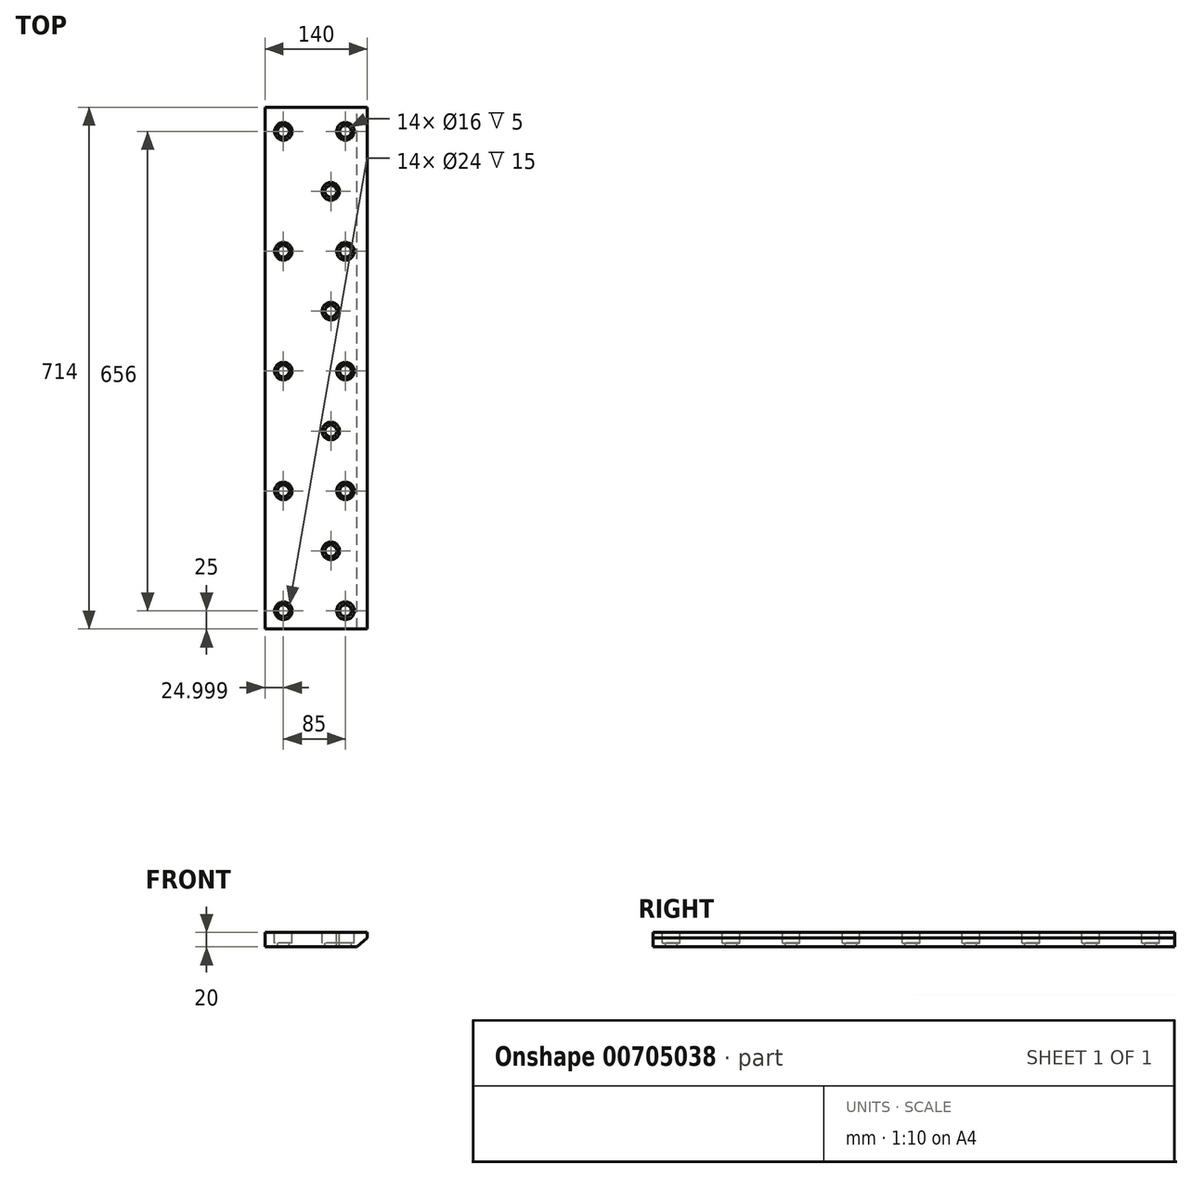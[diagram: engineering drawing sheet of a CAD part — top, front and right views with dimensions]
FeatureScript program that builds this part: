
annotation { "Feature Type Name" : "Feature", "Feature Type Description" : "" }
export const myFeature = defineFeature(function(context is Context, id is Id, definition is map)
    precondition{}
    {
        {
            var Q0;
            Q0=qCreatedBy(makeId("Front.planeOp"),FACE);
            var sketch = newSketch(context, id + "F0", { "sketchPlane" : qUnion([Q0])});
            skLineSegment(sketch, "E0", {"start": v(-96.72, 31.12) * mm, "end": v(43.28, 31.12) * mm});
            skLineSegment(sketch, "E1", {"start": v(43.28, 31.12) * mm, "end": v(43.28, 23.12) * mm});
            skLineSegment(sketch, "E2", {"start": v(43.28, 23.12) * mm, "end": v(28.98, 11.12) * mm});
            skLineSegment(sketch, "E3", {"start": v(28.98, 11.12) * mm, "end": v(-96.72, 11.12) * mm});
            skLineSegment(sketch, "E4", {"start": v(-96.72, 11.12) * mm, "end": v(-96.72, 31.12) * mm});
            skSolve(sketch);
        }
        {
            var Q0;
            Q0=makeQuery(id+"F0.imprint","IMPRINT",FACE,{"disambiguationData":[TD([[makeQuery(id+"F0.imprint","IMPRINT",EDGE,{"derivedFrom":sQuery(id+"F0.wireOp",EDGE,"E0")}),-1.0]])]});
            extrude(context, id + "F1", {"entities" : qUnion([Q0]), "depth" : 714 * mm, "offsetDistance" : 25 * mm});
        }
        {
            var Q0;
            Q0=makeQuery(id+"F1.opExtrude","SWEPT_FACE",FACE,{"disambiguationData":[OSD([sQuery(id+"F0.wireOp",EDGE,"E0")])]});
            var sketch = newSketch(context, id + "F2", { "sketchPlane" : qUnion([Q0])});
            skCircle(sketch, "E5", {"center": v(13.28, -689) * mm, "radius": 8 * mm});
            skCircle(sketch, "E6", {"center": v(-71.72, -689) * mm, "radius": 8 * mm});
            skCircle(sketch, "E7", {"center": v(-6.72, -607) * mm, "radius": 8 * mm});
            skCircle(sketch, "E8", {"center": v(13.28, -525) * mm, "radius": 8 * mm});
            skCircle(sketch, "E9", {"center": v(13.28, -361) * mm, "radius": 8 * mm});
            skCircle(sketch, "E10", {"center": v(13.28, -197) * mm, "radius": 8 * mm});
            skCircle(sketch, "E11", {"center": v(13.28, -33) * mm, "radius": 8 * mm});
            skCircle(sketch, "E12", {"center": v(-6.72, -443) * mm, "radius": 8 * mm});
            skCircle(sketch, "E13", {"center": v(-6.72, -279) * mm, "radius": 8 * mm});
            skCircle(sketch, "E14", {"center": v(-6.72, -115) * mm, "radius": 8 * mm});
            skCircle(sketch, "E15", {"center": v(-71.72, -525) * mm, "radius": 8 * mm});
            skCircle(sketch, "E16", {"center": v(-71.72, -361) * mm, "radius": 8 * mm});
            skCircle(sketch, "E17", {"center": v(-71.72, -197) * mm, "radius": 8 * mm});
            skCircle(sketch, "E18", {"center": v(-71.72, -33) * mm, "radius": 8 * mm});
            skCircle(sketch, "E19", {"center": v(13.28, -689) * mm, "radius": 12 * mm});
            skCircle(sketch, "E20", {"center": v(-71.72, -689) * mm, "radius": 12 * mm});
            skCircle(sketch, "E21", {"center": v(-6.72, -607) * mm, "radius": 12 * mm});
            skCircle(sketch, "E22", {"center": v(13.28, -525) * mm, "radius": 12 * mm});
            skCircle(sketch, "E23", {"center": v(-71.72, -525) * mm, "radius": 12 * mm});
            skCircle(sketch, "E24", {"center": v(-6.72, -443) * mm, "radius": 12 * mm});
            skCircle(sketch, "E25", {"center": v(13.28, -361) * mm, "radius": 12 * mm});
            skCircle(sketch, "E26", {"center": v(-71.72, -361) * mm, "radius": 12 * mm});
            skCircle(sketch, "E27", {"center": v(-6.72, -279) * mm, "radius": 12 * mm});
            skCircle(sketch, "E28", {"center": v(-71.72, -197) * mm, "radius": 12 * mm});
            skCircle(sketch, "E29", {"center": v(13.28, -197) * mm, "radius": 12 * mm});
            skCircle(sketch, "E30", {"center": v(-6.72, -115) * mm, "radius": 12 * mm});
            skCircle(sketch, "E31", {"center": v(13.28, -33) * mm, "radius": 12 * mm});
            skCircle(sketch, "E32", {"center": v(-71.72, -33) * mm, "radius": 12 * mm});
            skSolve(sketch);
        }
        {
            var Q0;
            Q0=makeQuery(id+"F2.imprint","IMPRINT",FACE,{"disambiguationData":[TD([[makeQuery(id+"F2.imprint","IMPRINT",EDGE,{"derivedFrom":sQuery(id+"F2.wireOp",EDGE,"E5")}),1.0]])]});
            var Q1;
            Q1=makeQuery(id+"F2.imprint","IMPRINT",FACE,{"disambiguationData":[TD([[makeQuery(id+"F2.imprint","IMPRINT",EDGE,{"derivedFrom":sQuery(id+"F2.wireOp",EDGE,"E6")}),1.0]])]});
            var Q2;
            Q2=makeQuery(id+"F2.imprint","IMPRINT",FACE,{"disambiguationData":[TD([[makeQuery(id+"F2.imprint","IMPRINT",EDGE,{"derivedFrom":sQuery(id+"F2.wireOp",EDGE,"E7")}),1.0]])]});
            var Q3;
            Q3=makeQuery(id+"F2.imprint","IMPRINT",FACE,{"disambiguationData":[TD([[makeQuery(id+"F2.imprint","IMPRINT",EDGE,{"derivedFrom":sQuery(id+"F2.wireOp",EDGE,"E8")}),1.0]])]});
            var Q4;
            Q4=makeQuery(id+"F2.imprint","IMPRINT",FACE,{"disambiguationData":[TD([[makeQuery(id+"F2.imprint","IMPRINT",EDGE,{"derivedFrom":sQuery(id+"F2.wireOp",EDGE,"E15")}),1.0]])]});
            var Q5;
            Q5=makeQuery(id+"F2.imprint","IMPRINT",FACE,{"disambiguationData":[TD([[makeQuery(id+"F2.imprint","IMPRINT",EDGE,{"derivedFrom":sQuery(id+"F2.wireOp",EDGE,"E12")}),1.0]])]});
            var Q6;
            Q6=makeQuery(id+"F2.imprint","IMPRINT",FACE,{"disambiguationData":[TD([[makeQuery(id+"F2.imprint","IMPRINT",EDGE,{"derivedFrom":sQuery(id+"F2.wireOp",EDGE,"E9")}),1.0]])]});
            var Q7;
            Q7=makeQuery(id+"F2.imprint","IMPRINT",FACE,{"disambiguationData":[TD([[makeQuery(id+"F2.imprint","IMPRINT",EDGE,{"derivedFrom":sQuery(id+"F2.wireOp",EDGE,"E16")}),1.0]])]});
            var Q8;
            Q8=makeQuery(id+"F2.imprint","IMPRINT",FACE,{"disambiguationData":[TD([[makeQuery(id+"F2.imprint","IMPRINT",EDGE,{"derivedFrom":sQuery(id+"F2.wireOp",EDGE,"E13")}),1.0]])]});
            var Q9;
            Q9=makeQuery(id+"F2.imprint","IMPRINT",FACE,{"disambiguationData":[TD([[makeQuery(id+"F2.imprint","IMPRINT",EDGE,{"derivedFrom":sQuery(id+"F2.wireOp",EDGE,"E10")}),1.0]])]});
            var Q10;
            Q10=makeQuery(id+"F2.imprint","IMPRINT",FACE,{"disambiguationData":[TD([[makeQuery(id+"F2.imprint","IMPRINT",EDGE,{"derivedFrom":sQuery(id+"F2.wireOp",EDGE,"E17")}),1.0]])]});
            var Q11;
            Q11=makeQuery(id+"F2.imprint","IMPRINT",FACE,{"disambiguationData":[TD([[makeQuery(id+"F2.imprint","IMPRINT",EDGE,{"derivedFrom":sQuery(id+"F2.wireOp",EDGE,"E14")}),1.0]])]});
            var Q12;
            Q12=makeQuery(id+"F2.imprint","IMPRINT",FACE,{"disambiguationData":[TD([[makeQuery(id+"F2.imprint","IMPRINT",EDGE,{"derivedFrom":sQuery(id+"F2.wireOp",EDGE,"E11")}),1.0]])]});
            var Q13;
            Q13=makeQuery(id+"F2.imprint","IMPRINT",FACE,{"disambiguationData":[TD([[makeQuery(id+"F2.imprint","IMPRINT",EDGE,{"derivedFrom":sQuery(id+"F2.wireOp",EDGE,"E18")}),1.0]])]});
            extrude(context, id + "F3", {"entities" : qUnion([Q0, Q1, Q2, Q3, Q4, Q5, Q6, Q7, Q8, Q9, Q10, Q11, Q12, Q13]), "operationType" : NewBodyOperationType.REMOVE, "oppositeDirection" : true, "depth" : 20 * mm, "offsetDistance" : 25 * mm});
        }
        {
            var Q0;
            Q0=makeQuery(id+"F2.imprint","IMPRINT",FACE,{"disambiguationData":[TD([[makeQuery(id+"F2.imprint","IMPRINT",EDGE,{"derivedFrom":sQuery(id+"F2.wireOp",EDGE,"E6")}),-1.0]])]});
            var Q1;
            Q1=makeQuery(id+"F2.imprint","IMPRINT",FACE,{"disambiguationData":[TD([[makeQuery(id+"F2.imprint","IMPRINT",EDGE,{"derivedFrom":sQuery(id+"F2.wireOp",EDGE,"E5")}),-1.0]])]});
            var Q2;
            Q2=makeQuery(id+"F2.imprint","IMPRINT",FACE,{"disambiguationData":[TD([[makeQuery(id+"F2.imprint","IMPRINT",EDGE,{"derivedFrom":sQuery(id+"F2.wireOp",EDGE,"E7")}),-1.0]])]});
            var Q3;
            Q3=makeQuery(id+"F2.imprint","IMPRINT",FACE,{"disambiguationData":[TD([[makeQuery(id+"F2.imprint","IMPRINT",EDGE,{"derivedFrom":sQuery(id+"F2.wireOp",EDGE,"E8")}),-1.0]])]});
            var Q4;
            Q4=makeQuery(id+"F2.imprint","IMPRINT",FACE,{"disambiguationData":[TD([[makeQuery(id+"F2.imprint","IMPRINT",EDGE,{"derivedFrom":sQuery(id+"F2.wireOp",EDGE,"E15")}),-1.0]])]});
            var Q5;
            Q5=makeQuery(id+"F2.imprint","IMPRINT",FACE,{"disambiguationData":[TD([[makeQuery(id+"F2.imprint","IMPRINT",EDGE,{"derivedFrom":sQuery(id+"F2.wireOp",EDGE,"E12")}),-1.0]])]});
            var Q6;
            Q6=makeQuery(id+"F2.imprint","IMPRINT",FACE,{"disambiguationData":[TD([[makeQuery(id+"F2.imprint","IMPRINT",EDGE,{"derivedFrom":sQuery(id+"F2.wireOp",EDGE,"E9")}),-1.0]])]});
            var Q7;
            Q7=makeQuery(id+"F2.imprint","IMPRINT",FACE,{"disambiguationData":[TD([[makeQuery(id+"F2.imprint","IMPRINT",EDGE,{"derivedFrom":sQuery(id+"F2.wireOp",EDGE,"E16")}),-1.0]])]});
            var Q8;
            Q8=makeQuery(id+"F2.imprint","IMPRINT",FACE,{"disambiguationData":[TD([[makeQuery(id+"F2.imprint","IMPRINT",EDGE,{"derivedFrom":sQuery(id+"F2.wireOp",EDGE,"E13")}),-1.0]])]});
            var Q9;
            Q9=makeQuery(id+"F2.imprint","IMPRINT",FACE,{"disambiguationData":[TD([[makeQuery(id+"F2.imprint","IMPRINT",EDGE,{"derivedFrom":sQuery(id+"F2.wireOp",EDGE,"E10")}),-1.0]])]});
            var Q10;
            Q10=makeQuery(id+"F2.imprint","IMPRINT",FACE,{"disambiguationData":[TD([[makeQuery(id+"F2.imprint","IMPRINT",EDGE,{"derivedFrom":sQuery(id+"F2.wireOp",EDGE,"E17")}),-1.0]])]});
            var Q11;
            Q11=makeQuery(id+"F2.imprint","IMPRINT",FACE,{"disambiguationData":[TD([[makeQuery(id+"F2.imprint","IMPRINT",EDGE,{"derivedFrom":sQuery(id+"F2.wireOp",EDGE,"E14")}),-1.0]])]});
            var Q12;
            Q12=makeQuery(id+"F2.imprint","IMPRINT",FACE,{"disambiguationData":[TD([[makeQuery(id+"F2.imprint","IMPRINT",EDGE,{"derivedFrom":sQuery(id+"F2.wireOp",EDGE,"E11")}),-1.0]])]});
            var Q13;
            Q13=makeQuery(id+"F2.imprint","IMPRINT",FACE,{"disambiguationData":[TD([[makeQuery(id+"F2.imprint","IMPRINT",EDGE,{"derivedFrom":sQuery(id+"F2.wireOp",EDGE,"E18")}),-1.0]])]});
            extrude(context, id + "F4", {"entities" : qUnion([Q0, Q1, Q2, Q3, Q4, Q5, Q6, Q7, Q8, Q9, Q10, Q11, Q12, Q13]), "operationType" : NewBodyOperationType.REMOVE, "oppositeDirection" : true, "depth" : 15 * mm, "offsetDistance" : 25 * mm});
        }
    });
